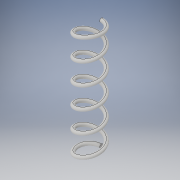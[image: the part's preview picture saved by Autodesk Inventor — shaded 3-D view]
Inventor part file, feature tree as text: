
AUTODESK INVENTOR PART (.ipt)
format: ipt  version: 2019 (Build 230136000, 136)  size: 441,856 bytes
history: native  units: in
note: dims shown in document units (in); Inventor stores cm internally (conversion verified against a paired STEP export)
features: helix x1, sketch x1
ambient origin geometry x8: Origin, YZ Plane, XZ Plane, XY Plane, X Axis, Y Axis, Z Axis, Center Point
bodies: Solid1 (feature_tree)
feature tree (2):
  helix  "Coil1"  [1 undecoded]
  sketch  "Sketch1"  dims[d1=0.0787in d2=1.7717in d3=0.3937in d4=2.3622in d5=1.9685in d6=0.0in d7=90.0deg d8=90.0deg d9=90.0deg d10=90.0deg]
note: 1 required parameter value undecoded (feature->parameter linkage not recoverable at this tier; creation-order binding heuristic only, values carry confidence <= 0.55)
